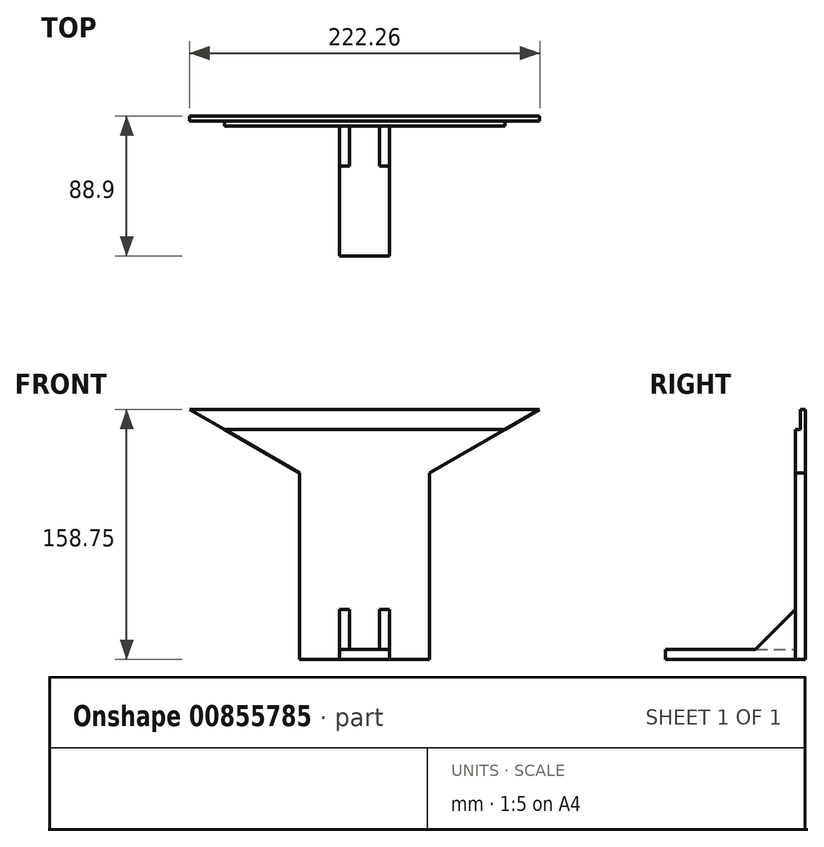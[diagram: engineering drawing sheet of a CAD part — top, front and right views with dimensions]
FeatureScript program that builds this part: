
annotation { "Feature Type Name" : "Feature", "Feature Type Description" : "" }
export const myFeature = defineFeature(function(context is Context, id is Id, definition is map)
    precondition{}
    {
        {
            var Q0;
            Q0=qCreatedBy(makeId("Front.planeOp"),FACE);
            var sketch = newSketch(context, id + "F0", { "sketchPlane" : qUnion([Q0])});
            skLineSegment(sketch, "E0.bottom", {"start": v(-41.28, 104.78) * mm, "end": v(0, 104.78) * mm});
            skLineSegment(sketch, "E0.top", {"start": v(-41.28, -53.98) * mm, "end": v(0, -53.98) * mm});
            skLineSegment(sketch, "E0.left", {"start": v(-41.28, 104.78) * mm, "end": v(-41.28, -53.98) * mm});
            skLineSegment(sketch, "E0.right", {"start": v(0, 104.78) * mm, "end": v(0, -53.98) * mm});
            skLineSegment(sketch, "E1", {"start": v(-41.28, 104.78) * mm, "end": v(-111.13, 104.78) * mm});
            skLineSegment(sketch, "E2", {"start": v(-111.13, 104.78) * mm, "end": v(-41.27, 64.45) * mm});
            skSolve(sketch);
        }
        {
            var Q0;
            {var subQ0=sQuery(id+"F0.wireOp",EDGE,"E1");Q0=makeQuery(id+"F0.imprint","IMPRINT",FACE,{"disambiguationData":[TD([[makeQuery(id+"F0.imprint","IMPRINT",EDGE,{"derivedFrom":subQ0}),1.0]])]});}
            var Q1;
            {var subQ3=sQuery(id+"F0.wireOp",EDGE,"E0.bottom");Q1=makeQuery(id+"F0.imprint","IMPRINT",FACE,{"disambiguationData":[TD([[makeQuery(id+"F0.imprint","IMPRINT",EDGE,{"derivedFrom":subQ3}),-1.0]])]});}
            extrude(context, id + "F1", {"entities" : qUnion([Q0, Q1]), "oppositeDirection" : true, "depth" : 6.35 * mm, "offsetDistance" : 25.4 * mm});
        }
        {
            var Q0;
            Q0=makeQuery(id+"F1.opExtrude","SWEPT_BODY",BODY,{"disambiguationData":[OSD([sQuery(id+"F0.wireOp",EDGE,"E0.bottom"),sQuery(id+"F0.wireOp",EDGE,"E0.top"),sQuery(id+"F0.wireOp",EDGE,"E0.left"),sQuery(id+"F0.wireOp",EDGE,"E0.right"),sQuery(id+"F0.wireOp",EDGE,"E1"),sQuery(id+"F0.wireOp",EDGE,"E2")])]});
            var Q1;
            Q1=qCreatedBy(makeId("Right.planeOp"),FACE);
            mirror(context, id + "F2", {"operationType" : NewBodyOperationType.ADD, "entities" : qUnion([Q0]), "mirrorPlane" : qUnion([Q1])});
        }
        {
            var Q0;
            Q0=qCreatedBy(makeId("Front.planeOp"),FACE);
            var sketch = newSketch(context, id + "F3", { "sketchPlane" : qUnion([Q0])});
            skLineSegment(sketch, "E3.bottom", {"start": v(-15.88, -47.62) * mm, "end": v(15.88, -47.62) * mm});
            skLineSegment(sketch, "E3.top", {"start": v(-15.88, -53.98) * mm, "end": v(15.88, -53.98) * mm});
            skLineSegment(sketch, "E3.left", {"start": v(-15.88, -47.62) * mm, "end": v(-15.88, -53.98) * mm});
            skLineSegment(sketch, "E3.right", {"start": v(15.88, -47.62) * mm, "end": v(15.88, -53.98) * mm});
            skSolve(sketch);
        }
        {
            var Q0;
            Q0=qSketchRegion(id+"F3",true);
            extrude(context, id + "F4", {"entities" : qUnion([Q0]), "operationType" : NewBodyOperationType.ADD, "depth" : 82.55 * mm, "offsetDistance" : 25.4 * mm});
        }
        {
            var Q0;
            Q0=makeQuery(id+"F4.opExtrude","SWEPT_FACE",FACE,{"disambiguationData":[OSD([sQuery(id+"F3.wireOp",EDGE,"E3.right")])]});
            var sketch = newSketch(context, id + "F5", { "sketchPlane" : qUnion([Q0])});
            skLineSegment(sketch, "E4", {"start": v(-25.4, -47.62) * mm, "end": v(0, -22.22) * mm});
            skLineSegment(sketch, "E5", {"start": v(0, -22.22) * mm, "end": v(0, -47.62) * mm});
            skLineSegment(sketch, "E6", {"start": v(0, -47.62) * mm, "end": v(-25.4, -47.62) * mm});
            skSolve(sketch);
        }
        {
            var Q0;
            Q0=qSketchRegion(id+"F5",true);
            extrude(context, id + "F6", {"entities" : qUnion([Q0]), "operationType" : NewBodyOperationType.ADD, "oppositeDirection" : true, "depth" : 6.35 * mm, "offsetDistance" : 25.4 * mm});
        }
        {
            var Q0;
            Q0=makeQuery(id+"F1.opExtrude","SWEPT_BODY",BODY,{"disambiguationData":[OSD([sQuery(id+"F0.wireOp",EDGE,"E0.bottom"),sQuery(id+"F0.wireOp",EDGE,"E0.top"),sQuery(id+"F0.wireOp",EDGE,"E0.left"),sQuery(id+"F0.wireOp",EDGE,"E0.right"),sQuery(id+"F0.wireOp",EDGE,"E1"),sQuery(id+"F0.wireOp",EDGE,"E2")])]});
            var Q1;
            Q1=qCreatedBy(makeId("Right.planeOp"),FACE);
            mirror(context, id + "F7", {"operationType" : NewBodyOperationType.ADD, "entities" : qUnion([Q0]), "mirrorPlane" : qUnion([Q1])});
        }
        {
            var Q0;
            Q0=qCreatedBy(makeId("Right.planeOp"),FACE);
            cPlane(context, id + "F8", {"entities" : qUnion([Q0]), "cplaneType" : CPlaneType.OFFSET, "offset" : 111.12 * mm, "width" : 152.4 * mm, "height" : 152.4 * mm});
        }
        {
            var Q0;
            Q0=qCreatedBy(id+"F8.planeOp",FACE);
            var sketch = newSketch(context, id + "F9", { "sketchPlane" : qUnion([Q0])});
            skLineSegment(sketch, "E7.bottom", {"start": v(0, 104.78) * mm, "end": v(3.18, 104.78) * mm});
            skLineSegment(sketch, "E7.top", {"start": v(0, 92.08) * mm, "end": v(3.18, 92.08) * mm});
            skLineSegment(sketch, "E7.left", {"start": v(0, 104.78) * mm, "end": v(0, 92.08) * mm});
            skLineSegment(sketch, "E7.right", {"start": v(3.18, 104.78) * mm, "end": v(3.18, 92.08) * mm});
            skSolve(sketch);
        }
        {
            var Q0;
            Q0 = qSketchRegion(id + "F9", true);
            extrude(context, id + "F10", {"entities" : qUnion([Q0]), "operationType" : NewBodyOperationType.REMOVE, "oppositeDirection" : true, "depth" : 222.25 * mm, "offsetDistance" : 25.4 * mm});
        }
    });
